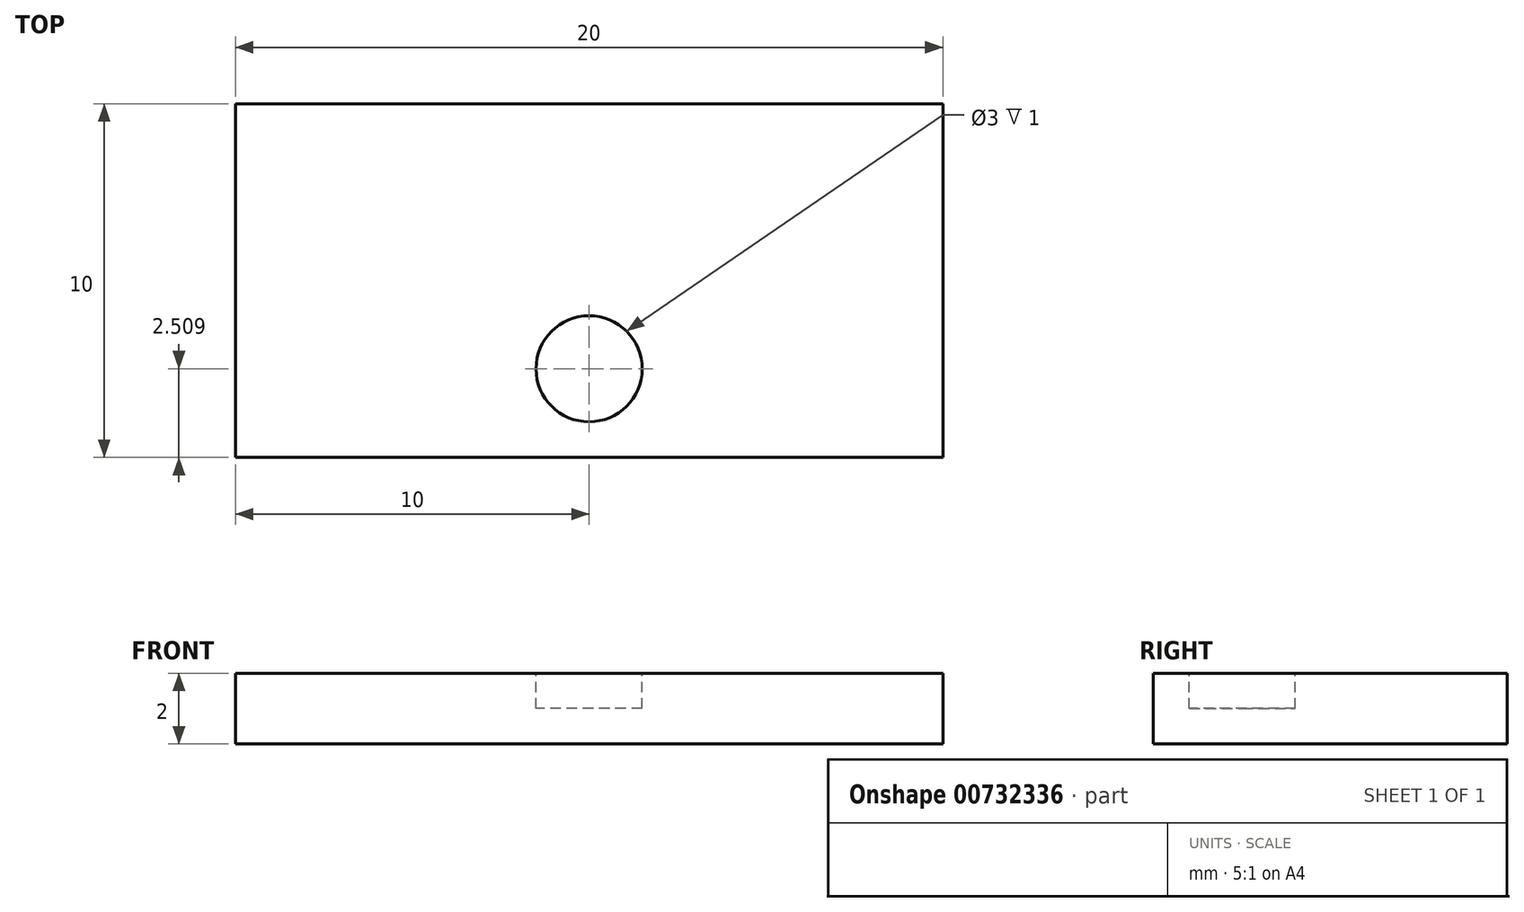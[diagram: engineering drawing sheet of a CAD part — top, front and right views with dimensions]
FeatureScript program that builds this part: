
annotation { "Feature Type Name" : "Feature", "Feature Type Description" : "" }
export const myFeature = defineFeature(function(context is Context, id is Id, definition is map)
    precondition{}
    {
        {
            var Q0;
            Q0=qCreatedBy(makeId("Top.planeOp"),FACE);
            var sketch = newSketch(context, id + "F0", { "sketchPlane" : qUnion([Q0])});
            skLineSegment(sketch, "E0.bottom", {"start": v(-35.67, -20.7) * mm, "end": v(-15.67, -20.7) * mm});
            skLineSegment(sketch, "E0.top", {"start": v(-35.67, -30.7) * mm, "end": v(-15.67, -30.7) * mm});
            skLineSegment(sketch, "E0.left", {"start": v(-35.67, -20.7) * mm, "end": v(-35.67, -30.7) * mm});
            skLineSegment(sketch, "E0.right", {"start": v(-15.67, -20.7) * mm, "end": v(-15.67, -30.7) * mm});
            skSolve(sketch);
        }
        {
            var Q0;
            Q0 = qSketchRegion(id + "F0", true);
            extrude(context, id + "F1", {"entities" : qUnion([Q0]), "depth" : 2 * mm, "offsetDistance" : 25 * mm});
        }
        {
            var Q0;
            Q0=makeQuery(id+"F1.opExtrude","CAP_FACE",FACE,{"disambiguationData":[OSD([sQuery(id+"F0.wireOp",EDGE,"E0.bottom"),sQuery(id+"F0.wireOp",EDGE,"E0.top"),sQuery(id+"F0.wireOp",EDGE,"E0.left"),sQuery(id+"F0.wireOp",EDGE,"E0.right")])],"isStart":false});
            var sketch = newSketch(context, id + "F2", { "sketchPlane" : qUnion([Q0])});
            skPoint(sketch, "E1.startSnap0", {"position": v(-25.67, -20.7) * mm});
            skCircle(sketch, "E2", {"center": v(-25.67, -28.2) * mm, "radius": 1.5 * mm});
            skSolve(sketch);
        }
        {
            var Q0;
            Q0 = qSketchRegion(id + "F2", true);
            extrude(context, id + "F3", {"entities" : qUnion([Q0]), "operationType" : NewBodyOperationType.REMOVE, "oppositeDirection" : true, "depth" : 1 * mm, "offsetDistance" : 25 * mm});
        }
    });
